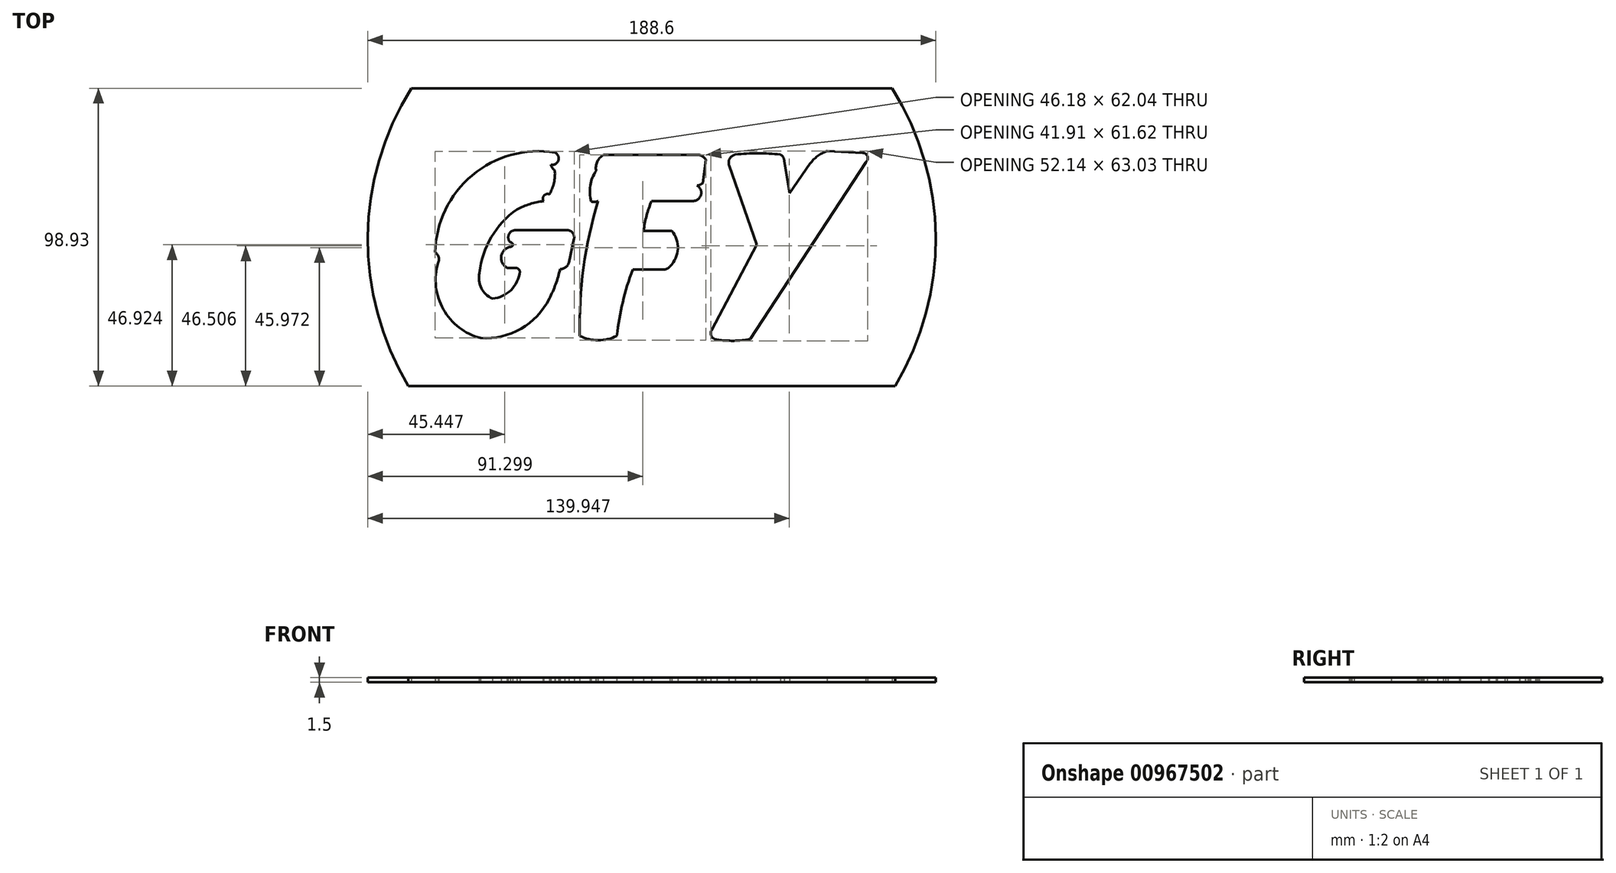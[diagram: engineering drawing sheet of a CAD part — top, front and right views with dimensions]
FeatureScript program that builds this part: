
annotation { "Feature Type Name" : "Feature", "Feature Type Description" : "" }
export const myFeature = defineFeature(function(context is Context, id is Id, definition is map)
    precondition{}
    {
        {
            var Q0;
            Q0=qCreatedBy(makeId("Top.planeOp"),FACE);
            var sketch = newSketch(context, id + "F0", { "sketchPlane" : qUnion([Q0])});
            skArc(sketch, "E0", {"start": v(83.51, -28.98) * mm, "mid": v(97.02, 20.63) * mm, "end": v(82.49, 69.95) * mm});
            skArc(sketch, "E1", {"start": v(-29.46, 48.6) * mm, "mid": v(-56.88, 41.01) * mm, "end": v(-69.22, 15.38) * mm});
            skArc(sketch, "E2", {"start": v(-68.22, 11.95) * mm, "mid": v(-68.07, 13.85) * mm, "end": v(-69.22, 15.38) * mm});
            skArc(sketch, "E3", {"start": v(-68.22, 11.95) * mm, "mid": v(-66.48, -3.57) * mm, "end": v(-54.1, -13.08) * mm});
            skArc(sketch, "E4", {"start": v(-54.1, -13.08) * mm, "mid": v(-40.72, -10) * mm, "end": v(-31.3, 0) * mm});
            skArc(sketch, "E5", {"start": v(-31.3, 0) * mm, "mid": v(-29.2, 4.8) * mm, "end": v(-27.72, 9.85) * mm});
            skArc(sketch, "E6", {"start": v(-27.72, 9.85) * mm, "mid": v(-25.9, 10.42) * mm, "end": v(-24.78, 11.95) * mm});
            skLineSegment(sketch, "E7", {"start": v(-24.78, 11.95) * mm, "end": v(-23.1, 19.84) * mm});
            skArc(sketch, "E8", {"start": v(-23.1, 19.84) * mm, "mid": v(-23.8, 22.14) * mm, "end": v(-26.14, 22.75) * mm});
            skLineSegment(sketch, "E9", {"start": v(-26.14, 22.75) * mm, "end": v(-42.58, 22.75) * mm});
            skArc(sketch, "E10", {"start": v(-42.58, 22.75) * mm, "mid": v(-44.76, 21.3) * mm, "end": v(-44.26, 18.74) * mm});
            skArc(sketch, "E11", {"start": v(-44.26, 17.25) * mm, "mid": v(-43.42, 18) * mm, "end": v(-44.26, 18.74) * mm});
            skArc(sketch, "E12", {"start": v(-44.26, 17.25) * mm, "mid": v(-47.25, 14.12) * mm, "end": v(-45.3, 10.26) * mm});
            skLineSegment(sketch, "E13", {"start": v(-45.3, 10.26) * mm, "end": v(-42.52, 10.26) * mm});
            skArc(sketch, "E14", {"start": v(-41.1, 9.1) * mm, "mid": v(-41.6, 9.93) * mm, "end": v(-42.52, 10.26) * mm});
            skArc(sketch, "E15", {"start": v(-50.22, 0) * mm, "mid": v(-44.02, 2.9) * mm, "end": v(-41.1, 9.1) * mm});
            skArc(sketch, "E16", {"start": v(-54.5, 8.58) * mm, "mid": v(-53.88, 3.53) * mm, "end": v(-50.22, 0) * mm});
            skArc(sketch, "E17", {"start": v(-42.06, 29.7) * mm, "mid": v(-50.55, 20.47) * mm, "end": v(-54.5, 8.58) * mm});
            skArc(sketch, "E18", {"start": v(-33.2, 32.45) * mm, "mid": v(-37.74, 31.44) * mm, "end": v(-42.06, 29.7) * mm});
            skArc(sketch, "E19", {"start": v(-30.8, 44.48) * mm, "mid": v(-28.32, 45.95) * mm, "end": v(-29.46, 48.6) * mm});
            skArc(sketch, "E20", {"start": v(-31.3, 34.7) * mm, "mid": v(-33.07, 34.26) * mm, "end": v(-33.2, 32.45) * mm});
            skArc(sketch, "E21", {"start": v(-30.8, 44.48) * mm, "mid": v(-30.3, 43.44) * mm, "end": v(-29.46, 42.64) * mm});
            skArc(sketch, "E22", {"start": v(-31.3, 34.7) * mm, "mid": v(-29.75, 38.52) * mm, "end": v(-29.46, 42.64) * mm});
            skArc(sketch, "E23", {"start": v(-15.12, 32.45) * mm, "mid": v(-19.94, 10.3) * mm, "end": v(-21.22, -12.35) * mm});
            skArc(sketch, "E24", {"start": v(-21.22, -12.35) * mm, "mid": v(-15.05, -13.82) * mm, "end": v(-8.87, -12.35) * mm});
            skArc(sketch, "E25", {"start": v(-3.56, 9.69) * mm, "mid": v(-6.92, -1.16) * mm, "end": v(-8.87, -12.35) * mm});
            skLineSegment(sketch, "E26", {"start": v(-3.56, 9.69) * mm, "end": v(6.6, 9.69) * mm});
            skArc(sketch, "E27", {"start": v(6.6, 9.69) * mm, "mid": v(7.83, 9.97) * mm, "end": v(8.8, 10.77) * mm});
            skArc(sketch, "E28", {"start": v(8.8, 10.77) * mm, "mid": v(11.38, 16.57) * mm, "end": v(9.33, 22.58) * mm});
            skLineSegment(sketch, "E29", {"start": v(9.33, 22.58) * mm, "end": v(0, 22.58) * mm});
            skArc(sketch, "E30", {"start": v(2.68, 32.46) * mm, "mid": v(1, 27.61) * mm, "end": v(0, 22.58) * mm});
            skLineSegment(sketch, "E31", {"start": v(2.68, 32.46) * mm, "end": v(16.41, 32.46) * mm});
            skArc(sketch, "E32", {"start": v(16.41, 32.46) * mm, "mid": v(19.08, 34.55) * mm, "end": v(17.7, 37.64) * mm});
            skArc(sketch, "E33", {"start": v(17.7, 37.64) * mm, "mid": v(18.72, 37.86) * mm, "end": v(19.6, 38.4) * mm});
            skLineSegment(sketch, "E34", {"start": v(19.6, 38.4) * mm, "end": v(20.68, 46.18) * mm});
            skArc(sketch, "E35", {"start": v(20.68, 46.18) * mm, "mid": v(19.38, 47.46) * mm, "end": v(17.58, 47.78) * mm});
            skLineSegment(sketch, "E36", {"start": v(17.58, 47.78) * mm, "end": v(-13.34, 47.78) * mm});
            skArc(sketch, "E37", {"start": v(-13.34, 47.78) * mm, "mid": v(-15.4, 45.51) * mm, "end": v(-15.76, 42.48) * mm});
            skArc(sketch, "E38", {"start": v(-15.76, 42.48) * mm, "mid": v(-17.7, 37.58) * mm, "end": v(-17.38, 32.33) * mm});
            skArc(sketch, "E39", {"start": v(-17.38, 32.33) * mm, "mid": v(-16.24, 32.16) * mm, "end": v(-15.12, 32.45) * mm});
            skLineSegment(sketch, "E40", {"start": v(22.55, -10.45) * mm, "end": v(37.62, 17.96) * mm});
            skLineSegment(sketch, "E41", {"start": v(37.62, 17.96) * mm, "end": v(28.4, 44.2) * mm});
            skArc(sketch, "E42", {"start": v(30.48, 47.9) * mm, "mid": v(28.6, 46.53) * mm, "end": v(28.4, 44.2) * mm});
            skArc(sketch, "E43", {"start": v(45.42, 47.9) * mm, "mid": v(37.95, 48.32) * mm, "end": v(30.48, 47.9) * mm});
            skArc(sketch, "E44", {"start": v(46.69, 45.64) * mm, "mid": v(46.39, 46.96) * mm, "end": v(45.42, 47.9) * mm});
            skLineSegment(sketch, "E45", {"start": v(46.69, 45.64) * mm, "end": v(48.55, 35.1) * mm});
            skLineSegment(sketch, "E46", {"start": v(48.55, 35.1) * mm, "end": v(55.29, 44.84) * mm});
            skArc(sketch, "E47", {"start": v(60.96, 49.04) * mm, "mid": v(57.78, 47.4) * mm, "end": v(55.29, 44.84) * mm});
            skLineSegment(sketch, "E48", {"start": v(60.96, 49.04) * mm, "end": v(72.73, 48.5) * mm});
            skArc(sketch, "E49", {"start": v(73.76, 45.33) * mm, "mid": v(74.35, 47.27) * mm, "end": v(72.73, 48.5) * mm});
            skLineSegment(sketch, "E50", {"start": v(73.76, 45.33) * mm, "end": v(35.47, -13.43) * mm});
            skArc(sketch, "E51", {"start": v(22.55, -10.45) * mm, "mid": v(22.57, -12.5) * mm, "end": v(24.32, -13.6) * mm});
            skArc(sketch, "E52", {"start": v(24.32, -13.6) * mm, "mid": v(29.9, -13.99) * mm, "end": v(35.47, -13.43) * mm});
            skLineSegment(sketch, "E53", {"start": v(-77.05, 69.95) * mm, "end": v(82.49, 69.95) * mm});
            skLineSegment(sketch, "E54", {"start": v(-78.07, -28.98) * mm, "end": v(83.51, -28.98) * mm});
            skArc(sketch, "E55.trimOffspring", {"start": v(-77.05, 69.95) * mm, "mid": v(-91.57, 20.63) * mm, "end": v(-78.07, -28.98) * mm});
            skSolve(sketch);
        }
        {
            var Q0;
            Q0=makeQuery(id+"F0.imprint","IMPRINT",FACE,{"disambiguationData":[TD([[makeQuery(id+"F0.imprint","IMPRINT",EDGE,{"derivedFrom":sQuery(id+"F0.wireOp",EDGE,"E0")}),1.0]])]});
            extrude(context, id + "F1", {"entities" : qUnion([Q0]), "depth" : 1.5 * mm, "offsetDistance" : 25 * mm});
        }
    });
